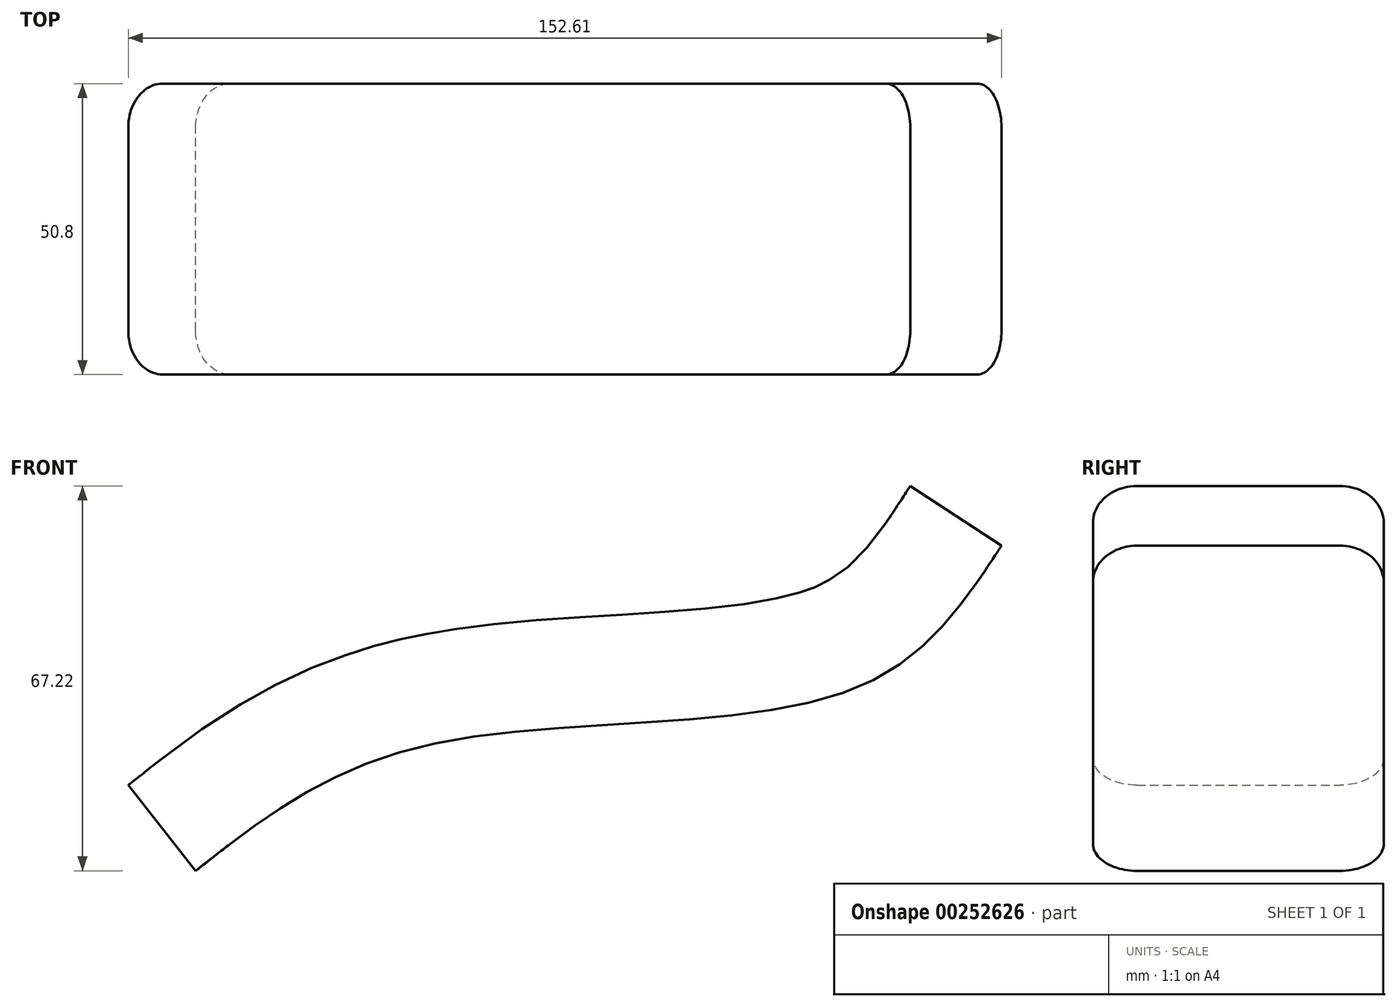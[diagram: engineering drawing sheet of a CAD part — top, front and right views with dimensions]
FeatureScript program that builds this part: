
annotation { "Feature Type Name" : "Feature", "Feature Type Description" : "" }
export const myFeature = defineFeature(function(context is Context, id is Id, definition is map)
    precondition{}
    {
        {
            var Q0;
            Q0=qCreatedBy(makeId("Front.planeOp"),FACE);
            var sketch = newSketch(context, id + "F0", { "sketchPlane" : qUnion([Q0])});
            skFitSpline(sketch, "E0", {"points": [v(-87.35, -14) * mm, v(-47, 7.93) * mm, v(27.03, 17.53) * mm, v(53.47, 42.8) * mm], "startDerivative": vector(108, 85.05) * mm, "endDerivative": vector(70.11, 107.32) * mm});
            skFitSpline(sketch, "E1.0", {"points": [v(-99.14, 0.96) * mm, v(-96.9, 2.73) * mm, v(-92.18, 6.45) * mm, v(-85.52, 11.27) * mm, v(-79.59, 15.04) * mm, v(-74.8, 17.76) * mm, v(-69.66, 20.32) * mm, v(-65.06, 22.26) * mm, v(-61.2, 23.67) * mm, v(-58.2, 24.65) * mm, v(-55.12, 25.55) * mm, v(-52.47, 26.23) * mm, v(-50.3, 26.72) * mm, v(-48.14, 27.17) * mm, v(-45.43, 27.68) * mm, v(-42.17, 28.2) * mm, v(-37.83, 28.8) * mm, v(-32.4, 29.39) * mm, v(-25.9, 29.93) * mm, v(-19.48, 30.35) * mm, v(-13.19, 30.73) * mm, v(-7.09, 31.1) * mm, v(-1.26, 31.53) * mm, v(4.22, 32.05) * mm, v(9.24, 32.68) * mm, v(12.95, 33.33) * mm, v(15.58, 33.9) * mm, v(17.35, 34.37) * mm, v(18.66, 34.77) * mm, v(19.6, 35.09) * mm, v(20.23, 35.32) * mm, v(20.83, 35.56) * mm, v(21.6, 35.9) * mm, v(22.49, 36.33) * mm, v(23.5, 36.89) * mm, v(24.75, 37.68) * mm, v(26.24, 38.8) * mm, v(27.97, 40.37) * mm, v(29.73, 42.25) * mm, v(31.54, 44.47) * mm, v(34.04, 47.9) * mm, v(36.06, 50.98) * mm, v(37.52, 53.22) * mm]});
            skLineSegment(sketch, "E2", {"start": v(-99.14, 0.96) * mm, "end": v(-87.35, -14) * mm});
            skLineSegment(sketch, "E3", {"start": v(37.52, 53.22) * mm, "end": v(53.47, 42.8) * mm});
            skSolve(sketch);
        }
        {
            var Q0;
            Q0 = qSketchRegion(id + "F0", true);
            var Q1;
            Q1=makeQuery(id+"F0.imprint","IMPRINT",FACE,{"disambiguationData":[TD([[makeQuery(id+"F0.imprint","IMPRINT",EDGE,{"derivedFrom":sQuery(id+"F0.wireOp",EDGE,"E0")}),1.0]])]});
            extrude(context, id + "F1", {"entities" : qUnion([Q0, Q1]), "depth" : 50.8 * mm});
        }
        {
            var Q0;
            Q0=makeQuery(id+"F1.opExtrude","CAP_EDGE",EDGE,{"disambiguationData":[OSD([sQuery(id+"F0.wireOp",EDGE,"E3")])],"isStart":false});
            var Q1;
            Q1=makeQuery(id+"F1.opExtrude","CAP_EDGE",EDGE,{"disambiguationData":[OSD([sQuery(id+"F0.wireOp",EDGE,"E2")])],"isStart":false});
            var Q2;
            Q2=makeQuery(id+"F1.opExtrude","CAP_EDGE",EDGE,{"disambiguationData":[OSD([sQuery(id+"F0.wireOp",EDGE,"E2")])],"isStart":true});
            var Q3;
            Q3=makeQuery(id+"F1.opExtrude","CAP_EDGE",EDGE,{"disambiguationData":[OSD([sQuery(id+"F0.wireOp",EDGE,"E3")])],"isStart":true});
            fillet(context, id + "F2", {"entities" : qUnion([Q0, Q1, Q2, Q3]), "radius" : 7.62 * mm, "tangentPropagation" : true, "allowEdgeOverflow" : false});
        }
    });
